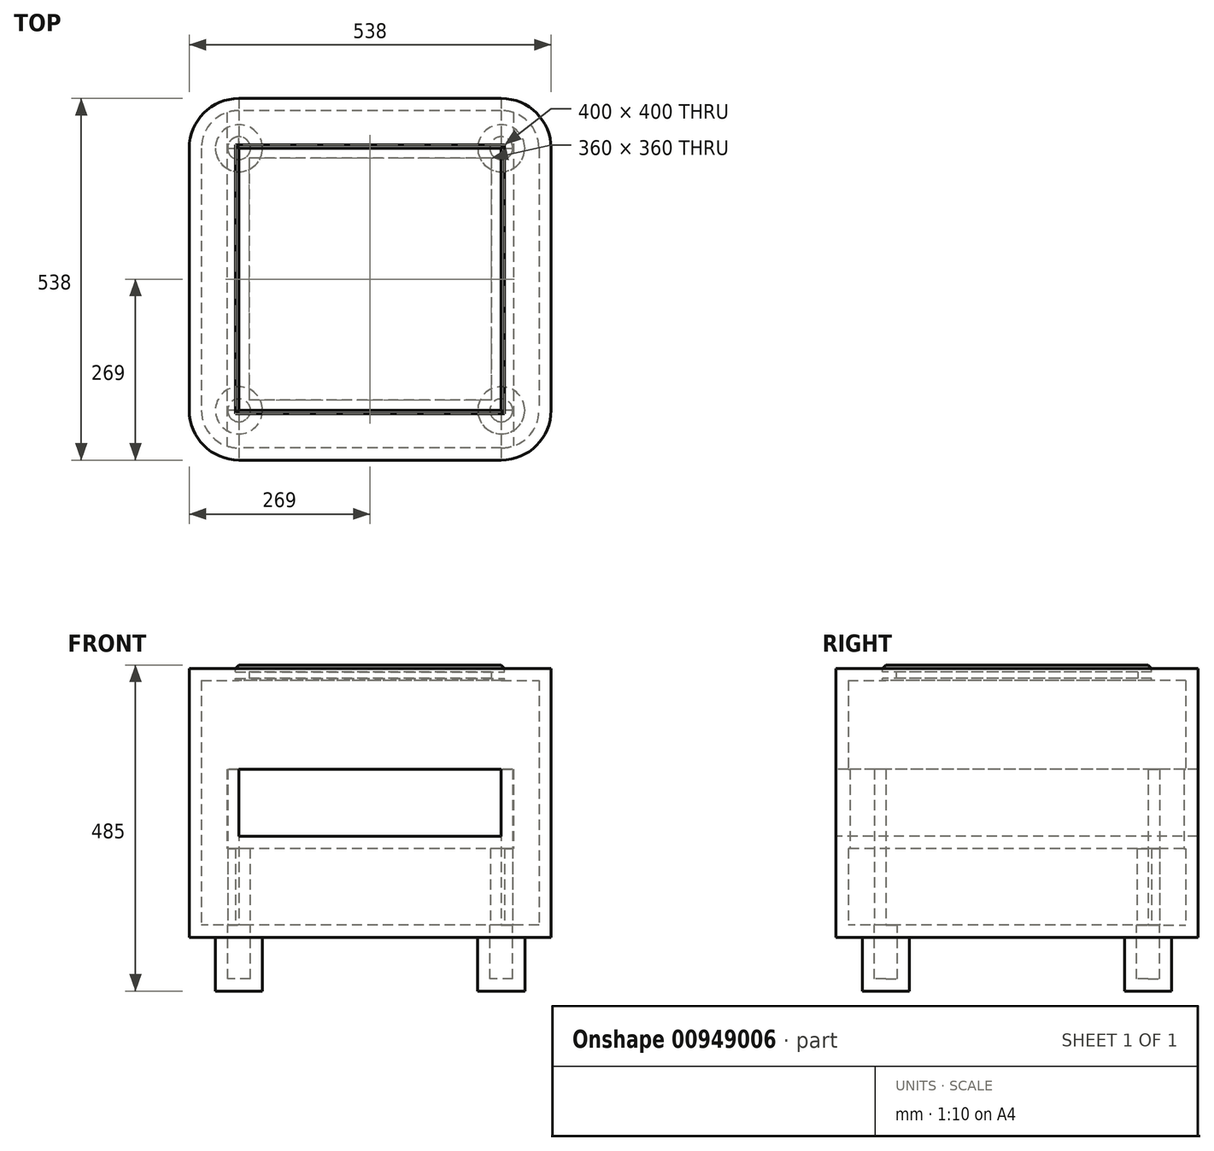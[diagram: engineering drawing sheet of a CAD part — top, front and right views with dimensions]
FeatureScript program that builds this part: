
annotation { "Feature Type Name" : "Feature", "Feature Type Description" : "" }
export const myFeature = defineFeature(function(context is Context, id is Id, definition is map)
    precondition{}
    {
        {
            var Q0;
            Q0=qCreatedBy(makeId("Top.planeOp"),FACE);
            var sketch = newSketch(context, id + "F0", { "sketchPlane" : qUnion([Q0])});
            skLineSegment(sketch, "E0.bottom", {"start": v(195, 269) * mm, "end": v(-195, 269) * mm});
            skLineSegment(sketch, "E0.top", {"start": v(195, -269) * mm, "end": v(-195, -269) * mm});
            skLineSegment(sketch, "E0.left", {"start": v(269, 195) * mm, "end": v(269, -195) * mm});
            skLineSegment(sketch, "E0.right", {"start": v(-269, 195) * mm, "end": v(-269, -195) * mm});
            skPoint(sketch, "E0.middle", {"position": v(0, 0) * mm});
            skPoint(sketch, "E1.visualSharp", {"position": v(-269, 269) * mm});
            skArc(sketch, "E1.filletArc", {"start": v(-195, 269) * mm, "mid": v(-247.33, 247.33) * mm, "end": v(-269, 195) * mm});
            skPoint(sketch, "E2.visualSharp", {"position": v(269, 269) * mm});
            skArc(sketch, "E2.filletArc", {"start": v(269, 195) * mm, "mid": v(247.33, 247.33) * mm, "end": v(195, 269) * mm});
            skPoint(sketch, "E3.visualSharp", {"position": v(269, -269) * mm});
            skArc(sketch, "E3.filletArc", {"start": v(195, -269) * mm, "mid": v(247.33, -247.33) * mm, "end": v(269, -195) * mm});
            skPoint(sketch, "E4.visualSharp", {"position": v(-269, -269) * mm});
            skArc(sketch, "E4.filletArc", {"start": v(-269, -195) * mm, "mid": v(-247.33, -247.33) * mm, "end": v(-195, -269) * mm});
            skSolve(sketch);
        }
        {
            var Q0;
            Q0=makeQuery(id+"F0.imprint","IMPRINT",FACE,{"disambiguationData":[TD([[makeQuery(id+"F0.imprint","IMPRINT",EDGE,{"derivedFrom":sQuery(id+"F0.wireOp",EDGE,"E0.bottom")}),1.0]])]});
            extrude(context, id + "F1", {"entities" : qUnion([Q0]), "depth" : 400 * mm, "offsetDistance" : 25 * mm});
        }
        {
            var Q0;
            Q0=makeQuery(id+"F1.opExtrude","CAP_FACE",FACE,{"disambiguationData":[OSD([sQuery(id+"F0.wireOp",EDGE,"E0.bottom"),sQuery(id+"F0.wireOp",EDGE,"E0.top"),sQuery(id+"F0.wireOp",EDGE,"E0.left"),sQuery(id+"F0.wireOp",EDGE,"E0.right"),sQuery(id+"F0.wireOp",EDGE,"E1.filletArc"),sQuery(id+"F0.wireOp",EDGE,"E2.filletArc"),sQuery(id+"F0.wireOp",EDGE,"E3.filletArc"),sQuery(id+"F0.wireOp",EDGE,"E4.filletArc")])],"isStart":true});
            var sketch = newSketch(context, id + "F2", { "sketchPlane" : qUnion([Q0])});
            skCircle(sketch, "E5", {"center": v(-195, 195) * mm, "radius": 35 * mm});
            skCircle(sketch, "E6", {"center": v(195, 195) * mm, "radius": 35 * mm});
            skCircle(sketch, "E7", {"center": v(-195, -195) * mm, "radius": 35 * mm});
            skCircle(sketch, "E8", {"center": v(195, -195) * mm, "radius": 35 * mm});
            skSolve(sketch);
        }
        {
            var Q0;
            Q0=makeQuery(id+"F2.imprint","IMPRINT",FACE,{"disambiguationData":[TD([[makeQuery(id+"F2.imprint","IMPRINT",EDGE,{"derivedFrom":sQuery(id+"F2.wireOp",EDGE,"E5")}),1.0]])]});
            var Q1;
            Q1=makeQuery(id+"F2.imprint","IMPRINT",FACE,{"disambiguationData":[TD([[makeQuery(id+"F2.imprint","IMPRINT",EDGE,{"derivedFrom":sQuery(id+"F2.wireOp",EDGE,"E6")}),1.0]])]});
            var Q2;
            Q2=makeQuery(id+"F2.imprint","IMPRINT",FACE,{"disambiguationData":[TD([[makeQuery(id+"F2.imprint","IMPRINT",EDGE,{"derivedFrom":sQuery(id+"F2.wireOp",EDGE,"E8")}),1.0]])]});
            var Q3;
            Q3=makeQuery(id+"F2.imprint","IMPRINT",FACE,{"disambiguationData":[TD([[makeQuery(id+"F2.imprint","IMPRINT",EDGE,{"derivedFrom":sQuery(id+"F2.wireOp",EDGE,"E7")}),1.0]])]});
            extrude(context, id + "F3", {"entities" : qUnion([Q0, Q1, Q2, Q3]), "operationType" : NewBodyOperationType.ADD, "depth" : 80 * mm, "offsetDistance" : 25 * mm});
        }
        {
            var Q0;
            Q0=makeQuery(id+"F1.opExtrude","SWEPT_FACE",FACE,{"disambiguationData":[OSD([sQuery(id+"F0.wireOp",EDGE,"E0.top")])]});
            var sketch = newSketch(context, id + "F4", { "sketchPlane" : qUnion([Q0])});
            skLineSegment(sketch, "E9.0", {"start": v(-269, 400) * mm, "end": v(-269, 0) * mm});
            skLineSegment(sketch, "E9.1", {"start": v(269, 400) * mm, "end": v(269, 0) * mm});
            skLineSegment(sketch, "E10.bottom", {"start": v(269, 250) * mm, "end": v(-269, 250) * mm});
            skLineSegment(sketch, "E10.top", {"start": v(269, 150) * mm, "end": v(-269, 150) * mm});
            skLineSegment(sketch, "E10.left", {"start": v(269, 250) * mm, "end": v(269, 150) * mm});
            skLineSegment(sketch, "E10.right", {"start": v(-269, 250) * mm, "end": v(-269, 150) * mm});
            skPoint(sketch, "E10.middle", {"position": v(0, 200) * mm});
            skPoint(sketch, "E10.middle.positionSnap0", {"position": v(-195, 200) * mm});
            skPoint(sketch, "E10.centerSnap0", {"position": v(-195, 200) * mm});
            skSolve(sketch);
        }
        {
            var Q0;
            {var subQ0=sQuery(id+"F4.wireOp",EDGE,"E10.right");Q0=makeQuery(id+"F4.imprint","IMPRINT",FACE,{"disambiguationData":[TD([[makeQuery(id+"F4.imprint","IMPRINT",EDGE,{"derivedFrom":subQ0}),1.0]])]});}
            var Q1;
            {var subQ0=sQuery(id+"F4.wireOp",EDGE,"E10.bottom");var subQ1=sQuery(id+"F0.wireOp",EDGE,"E0.top");var subQ2=makeQuery(id+"F1.opExtrude","SWEPT_EDGE",EDGE,{"disambiguationData":[OSD([subQ1,sQuery(id+"F0.wireOp",EDGE,"E3.filletArc")])]});var subQ3=makeQuery(id+"F4.imprint","INTERSECT",VERTEX,{"derivedFrom":[subQ2,subQ0]});Q1=makeQuery(id+"F4.imprint","IMPRINT",FACE,{"disambiguationData":[TD([[makeQuery(id+"F4.imprint","IMPRINT",EDGE,{"disambiguationData":[TD([[subQ3,-1.0]])],"derivedFrom":subQ0}),1.0]])]});}
            var Q2;
            {var subQ0=sQuery(id+"F4.wireOp",EDGE,"E10.left");Q2=makeQuery(id+"F4.imprint","IMPRINT",FACE,{"disambiguationData":[TD([[makeQuery(id+"F4.imprint","IMPRINT",EDGE,{"derivedFrom":subQ0}),-1.0]])]});}
            extrude(context, id + "F5", {"entities" : qUnion([Q0, Q1, Q2]), "operationType" : NewBodyOperationType.REMOVE, "endBound" : BoundingType.THROUGH_ALL, "oppositeDirection" : true, "depth" : 25 * mm, "offsetDistance" : 25 * mm});
        }
        {
            var Q0;
            Q0=makeQuery(id+"F5.boolean.opBoolean","COPY",FACE,{"derivedFrom":makeQuery(id+"F5.opExtrude","SWEPT_FACE",FACE,{"disambiguationData":[OSD([sQuery(id+"F4.wireOp",EDGE,"E10.bottom")])]})});
            shell(context, id + "F6", {"entities" : qUnion([Q0]), "thickness" : 18 * mm});
        }
        {
            var Q0;
            Q0=makeQuery(id+"F1.opExtrude","CAP_FACE",FACE,{"disambiguationData":[OSD([sQuery(id+"F0.wireOp",EDGE,"E0.bottom"),sQuery(id+"F0.wireOp",EDGE,"E0.top"),sQuery(id+"F0.wireOp",EDGE,"E0.left"),sQuery(id+"F0.wireOp",EDGE,"E0.right"),sQuery(id+"F0.wireOp",EDGE,"E1.filletArc"),sQuery(id+"F0.wireOp",EDGE,"E2.filletArc"),sQuery(id+"F0.wireOp",EDGE,"E3.filletArc"),sQuery(id+"F0.wireOp",EDGE,"E4.filletArc")])],"isStart":false});
            var sketch = newSketch(context, id + "F7", { "sketchPlane" : qUnion([Q0])});
            skLineSegment(sketch, "E11.bottom", {"start": v(200, 200) * mm, "end": v(-200, 200) * mm});
            skLineSegment(sketch, "E11.top", {"start": v(200, -200) * mm, "end": v(-200, -200) * mm});
            skLineSegment(sketch, "E11.left", {"start": v(200, 200) * mm, "end": v(200, -200) * mm});
            skLineSegment(sketch, "E11.right", {"start": v(-200, 200) * mm, "end": v(-200, -200) * mm});
            skPoint(sketch, "E11.middle", {"position": v(0, 0) * mm});
            skSolve(sketch);
        }
        {
            var Q0;
            Q0=makeQuery(id+"F7.imprint","IMPRINT",FACE,{"disambiguationData":[TD([[makeQuery(id+"F7.imprint","IMPRINT",EDGE,{"derivedFrom":sQuery(id+"F7.wireOp",EDGE,"E11.bottom")}),1.0]])]});
            extrude(context, id + "F8", {"entities" : qUnion([Q0]), "operationType" : NewBodyOperationType.REMOVE, "oppositeDirection" : true, "depth" : 25 * mm, "offsetDistance" : 25 * mm});
        }
        {
            var Q0;
            Q0=makeQuery(id+"F6.opShell","OFFSET_FACE",FACE,{"disambiguationData":[OSD([sQuery(id+"F0.wireOp",EDGE,"E0.bottom"),sQuery(id+"F0.wireOp",EDGE,"E0.top"),sQuery(id+"F0.wireOp",EDGE,"E0.left"),sQuery(id+"F0.wireOp",EDGE,"E0.right"),sQuery(id+"F0.wireOp",EDGE,"E1.filletArc"),sQuery(id+"F0.wireOp",EDGE,"E2.filletArc"),sQuery(id+"F0.wireOp",EDGE,"E3.filletArc"),sQuery(id+"F0.wireOp",EDGE,"E4.filletArc")])]});
            var sketch = newSketch(context, id + "F9", { "sketchPlane" : qUnion([Q0])});
            skLineSegment(sketch, "E12.bottom", {"start": v(200, 200) * mm, "end": v(-200, 200) * mm});
            skLineSegment(sketch, "E12.top", {"start": v(200, -200) * mm, "end": v(-200, -200) * mm});
            skLineSegment(sketch, "E12.left", {"start": v(200, 200) * mm, "end": v(200, -200) * mm});
            skLineSegment(sketch, "E12.right", {"start": v(-200, 200) * mm, "end": v(-200, -200) * mm});
            skPoint(sketch, "E12.middle", {"position": v(0, 0) * mm});
            skLineSegment(sketch, "E13.bottom", {"start": v(218, 218) * mm, "end": v(-218, 218) * mm});
            skLineSegment(sketch, "E13.top", {"start": v(218, -218) * mm, "end": v(-218, -218) * mm});
            skLineSegment(sketch, "E13.left", {"start": v(218, 218) * mm, "end": v(218, -218) * mm});
            skLineSegment(sketch, "E13.right", {"start": v(-218, 218) * mm, "end": v(-218, -218) * mm});
            skSolve(sketch);
        }
        {
            var Q0;
            Q0=makeQuery(id+"F9.imprint","IMPRINT",FACE,{"disambiguationData":[TD([[makeQuery(id+"F9.imprint","IMPRINT",EDGE,{"derivedFrom":sQuery(id+"F9.wireOp",EDGE,"E12.bottom")}),-1.0]])]});
            extrude(context, id + "F10", {"entities" : qUnion([Q0]), "endBound" : BoundingType.UP_TO_NEXT, "depth" : 25 * mm, "offsetDistance" : 25 * mm});
        }
        {
            var Q0;
            Q0=makeQuery(id+"F5.boolean.opBoolean","COPY",FACE,{"derivedFrom":makeQuery(id+"F5.opExtrude","SWEPT_FACE",FACE,{"disambiguationData":[OSD([sQuery(id+"F4.wireOp",EDGE,"E10.top")])]})});
            cPlane(context, id + "F11", {"entities" : qUnion([Q0]), "cplaneType" : CPlaneType.OFFSET, "offset" : 235 * mm, "width" : 150 * mm, "height" : 150 * mm});
        }
        {
            var Q0;
            Q0=qCreatedBy(id+"F11.planeOp",FACE);
            var sketch = newSketch(context, id + "F12", { "sketchPlane" : qUnion([Q0])});
            skLineSegment(sketch, "E14.0", {"start": v(-200, 200) * mm, "end": v(-200, -200) * mm});
            skLineSegment(sketch, "E15.0", {"start": v(200, 200) * mm, "end": v(200, -200) * mm});
            skLineSegment(sketch, "E16.bottom", {"start": v(-200, 200) * mm, "end": v(200, 200) * mm});
            skLineSegment(sketch, "E16.top", {"start": v(-200, -200) * mm, "end": v(200, -200) * mm});
            skPoint(sketch, "E16.middle", {"position": v(0, 0) * mm});
            skLineSegment(sketch, "E17.bottom", {"start": v(180, 180) * mm, "end": v(-180, 180) * mm});
            skLineSegment(sketch, "E17.top", {"start": v(180, -180) * mm, "end": v(-180, -180) * mm});
            skLineSegment(sketch, "E17.left", {"start": v(180, 180) * mm, "end": v(180, -180) * mm});
            skLineSegment(sketch, "E17.right", {"start": v(-180, 180) * mm, "end": v(-180, -180) * mm});
            skSolve(sketch);
        }
        {
            var Q0;
            Q0=makeQuery(id+"F12.imprint","IMPRINT",FACE,{"disambiguationData":[TD([[makeQuery(id+"F12.imprint","IMPRINT",EDGE,{"derivedFrom":sQuery(id+"F12.wireOp",EDGE,"E16.bottom")}),-1.0]])]});
            extrude(context, id + "F13", {"entities" : qUnion([Q0]), "operationType" : NewBodyOperationType.ADD, "depth" : 10 * mm, "offsetDistance" : 25 * mm});
        }
        {
            var Q0;
            Q0=makeQuery(id+"F13.opExtrude","CAP_FACE",FACE,{"disambiguationData":[OSD([sQuery(id+"F12.wireOp",EDGE,"E16.bottom"),sQuery(id+"F12.wireOp",EDGE,"E16.top"),sQuery(id+"F12.wireOp",EDGE,"E14.0"),sQuery(id+"F12.wireOp",EDGE,"E15.0"),sQuery(id+"F12.wireOp",EDGE,"E17.bottom"),sQuery(id+"F12.wireOp",EDGE,"E17.top"),sQuery(id+"F12.wireOp",EDGE,"E17.left"),sQuery(id+"F12.wireOp",EDGE,"E17.right")])],"isStart":false});
            var sketch = newSketch(context, id + "F14", { "sketchPlane" : qUnion([Q0])});
            skLineSegment(sketch, "E18.bottom", {"start": v(200, 200) * mm, "end": v(-200, 200) * mm});
            skLineSegment(sketch, "E18.top", {"start": v(200, -200) * mm, "end": v(-200, -200) * mm});
            skLineSegment(sketch, "E18.left", {"start": v(200, 200) * mm, "end": v(200, -200) * mm});
            skLineSegment(sketch, "E18.right", {"start": v(-200, 200) * mm, "end": v(-200, -200) * mm});
            skPoint(sketch, "E18.middle", {"position": v(0, 0) * mm});
            skSolve(sketch);
        }
        {
            var Q0;
            Q0=makeQuery(id+"F14.imprint","IMPRINT",FACE,{"disambiguationData":[TD([[makeQuery(id+"F14.imprint","IMPRINT",EDGE,{"derivedFrom":sQuery(id+"F14.wireOp",EDGE,"E18.bottom")}),-1.0]])]});
            var Q1;
            Q1=makeQuery(id+"F14.imprint","IMPRINT",FACE,{"disambiguationData":[TD([[makeQuery(id+"F14.imprint","IMPRINT",EDGE,{"derivedFrom":makeQuery(id+"F13.opExtrude","CAP_EDGE",EDGE,{"disambiguationData":[OSD([sQuery(id+"F12.wireOp",EDGE,"E17.bottom")])],"isStart":false})}),1.0]])]});
            extrude(context, id + "F15", {"entities" : qUnion([Q0, Q1]), "depth" : 10 * mm, "offsetDistance" : 25 * mm});
        }
        {
            var Q0;
            Q0=makeQuery(id+"F15.opExtrude","CAP_EDGE",EDGE,{"disambiguationData":[OSD([sQuery(id+"F14.wireOp",EDGE,"E18.right")])],"isStart":false});
            var Q1;
            Q1=makeQuery(id+"F15.opExtrude","CAP_EDGE",EDGE,{"disambiguationData":[OSD([sQuery(id+"F14.wireOp",EDGE,"E18.top")])],"isStart":false});
            var Q2;
            Q2=makeQuery(id+"F15.opExtrude","CAP_EDGE",EDGE,{"disambiguationData":[OSD([sQuery(id+"F14.wireOp",EDGE,"E18.bottom")])],"isStart":false});
            var Q3;
            Q3=makeQuery(id+"F15.opExtrude","CAP_EDGE",EDGE,{"disambiguationData":[OSD([sQuery(id+"F14.wireOp",EDGE,"E18.left")])],"isStart":false});
            chamfer(context, id + "F16", {"entities" : qUnion([Q0, Q1, Q2, Q3]), "width" : 5 * mm, "tangentPropagation" : true});
        }
        {
            var Q0;
            Q0=makeQuery(id+"F6.opShell","OFFSET_FACE",FACE,{"disambiguationData":[OSD([sQuery(id+"F0.wireOp",EDGE,"E0.bottom"),sQuery(id+"F0.wireOp",EDGE,"E0.top"),sQuery(id+"F0.wireOp",EDGE,"E0.left"),sQuery(id+"F0.wireOp",EDGE,"E0.right"),sQuery(id+"F0.wireOp",EDGE,"E1.filletArc"),sQuery(id+"F0.wireOp",EDGE,"E2.filletArc"),sQuery(id+"F0.wireOp",EDGE,"E3.filletArc"),sQuery(id+"F0.wireOp",EDGE,"E4.filletArc")])]});
            var sketch = newSketch(context, id + "F17", { "sketchPlane" : qUnion([Q0])});
            skLineSegment(sketch, "E19", {"start": v(-251, 195) * mm, "end": v(-195, 195) * mm});
            skLineSegment(sketch, "E20", {"start": v(-195, 195) * mm, "end": v(-195, 251) * mm});
            skArc(sketch, "E21.0", {"start": v(-251, 195) * mm, "mid": v(-234.6, 234.6) * mm, "end": v(-195, 251) * mm});
            skArc(sketch, "E22", {"start": v(-195, 251) * mm, "mid": v(-234.6, 234.6) * mm, "end": v(-251, 195) * mm});
            skLineSegment(sketch, "E23", {"start": v(195, 251) * mm, "end": v(195, 195) * mm});
            skLineSegment(sketch, "E24", {"start": v(195, 195) * mm, "end": v(251, 195) * mm});
            skLineSegment(sketch, "E25", {"start": v(251, -195) * mm, "end": v(195, -195) * mm});
            skLineSegment(sketch, "E26", {"start": v(195, -195) * mm, "end": v(195, -251) * mm});
            skLineSegment(sketch, "E27", {"start": v(-195, -195) * mm, "end": v(-251, -195) * mm});
            skLineSegment(sketch, "E28", {"start": v(-195, -195) * mm, "end": v(-195, -251) * mm});
            skArc(sketch, "E29", {"start": v(-251, -195) * mm, "mid": v(-234.6, -234.6) * mm, "end": v(-195, -251) * mm});
            skArc(sketch, "E30", {"start": v(195, -251) * mm, "mid": v(234.6, -234.6) * mm, "end": v(251, -195) * mm});
            skArc(sketch, "E31", {"start": v(251, 195) * mm, "mid": v(234.6, 234.6) * mm, "end": v(195, 251) * mm});
            skSolve(sketch);
        }
        {
            var Q0;
            Q0=makeQuery(id+"F17.imprint","IMPRINT",FACE,{"disambiguationData":[TD([[makeQuery(id+"F17.imprint","IMPRINT",EDGE,{"derivedFrom":sQuery(id+"F17.wireOp",EDGE,"E19")}),1.0]])]});
            var Q1;
            Q1=makeQuery(id+"F17.imprint","IMPRINT",FACE,{"disambiguationData":[TD([[makeQuery(id+"F17.imprint","IMPRINT",EDGE,{"derivedFrom":sQuery(id+"F17.wireOp",EDGE,"E23")}),1.0]])]});
            var Q2;
            Q2=makeQuery(id+"F17.imprint","IMPRINT",FACE,{"disambiguationData":[TD([[makeQuery(id+"F17.imprint","IMPRINT",EDGE,{"derivedFrom":sQuery(id+"F17.wireOp",EDGE,"E25")}),1.0]])]});
            var Q3;
            Q3=makeQuery(id+"F17.imprint","IMPRINT",FACE,{"disambiguationData":[TD([[makeQuery(id+"F17.imprint","IMPRINT",EDGE,{"derivedFrom":sQuery(id+"F17.wireOp",EDGE,"E27")}),1.0]])]});
            var Q4;
            {var subQ8=sQuery(id+"F17.wireOp",EDGE,"E31");Q4=makeQuery(id+"F17.imprint","IMPRINT",FACE,{"disambiguationData":[TD([[makeQuery(id+"F17.imprint","IMPRINT",EDGE,{"derivedFrom":subQ8}),-1.0]])]});}
            var Q5;
            {var subQ0=sQuery(id+"F17.wireOp",EDGE,"E22");Q5=makeQuery(id+"F17.imprint","IMPRINT",FACE,{"disambiguationData":[TD([[makeQuery(id+"F17.imprint","IMPRINT",EDGE,{"derivedFrom":subQ0}),-1.0]])]});}
            var Q6;
            {var subQ8=sQuery(id+"F17.wireOp",EDGE,"E29");Q6=makeQuery(id+"F17.imprint","IMPRINT",FACE,{"disambiguationData":[TD([[makeQuery(id+"F17.imprint","IMPRINT",EDGE,{"derivedFrom":subQ8}),-1.0]])]});}
            var Q7;
            {var subQ0=sQuery(id+"F17.wireOp",EDGE,"E30");Q7=makeQuery(id+"F17.imprint","IMPRINT",FACE,{"disambiguationData":[TD([[makeQuery(id+"F17.imprint","IMPRINT",EDGE,{"derivedFrom":subQ0}),-1.0]])]});}
            var Q8;
            Q8=makeQuery(id+"F5.boolean.opBoolean","COPY",FACE,{"derivedFrom":makeQuery(id+"F5.opExtrude","SWEPT_FACE",FACE,{"disambiguationData":[OSD([sQuery(id+"F4.wireOp",EDGE,"E10.bottom")])]})});
            extrude(context, id + "F18", {"entities" : qUnion([Q0, Q1, Q2, Q3, Q4, Q5, Q6, Q7]), "endBound" : BoundingType.UP_TO_SURFACE, "depth" : 25 * mm, "endBoundEntityFace" : qUnion([Q8]), "offsetDistance" : 25 * mm});
        }
    });
